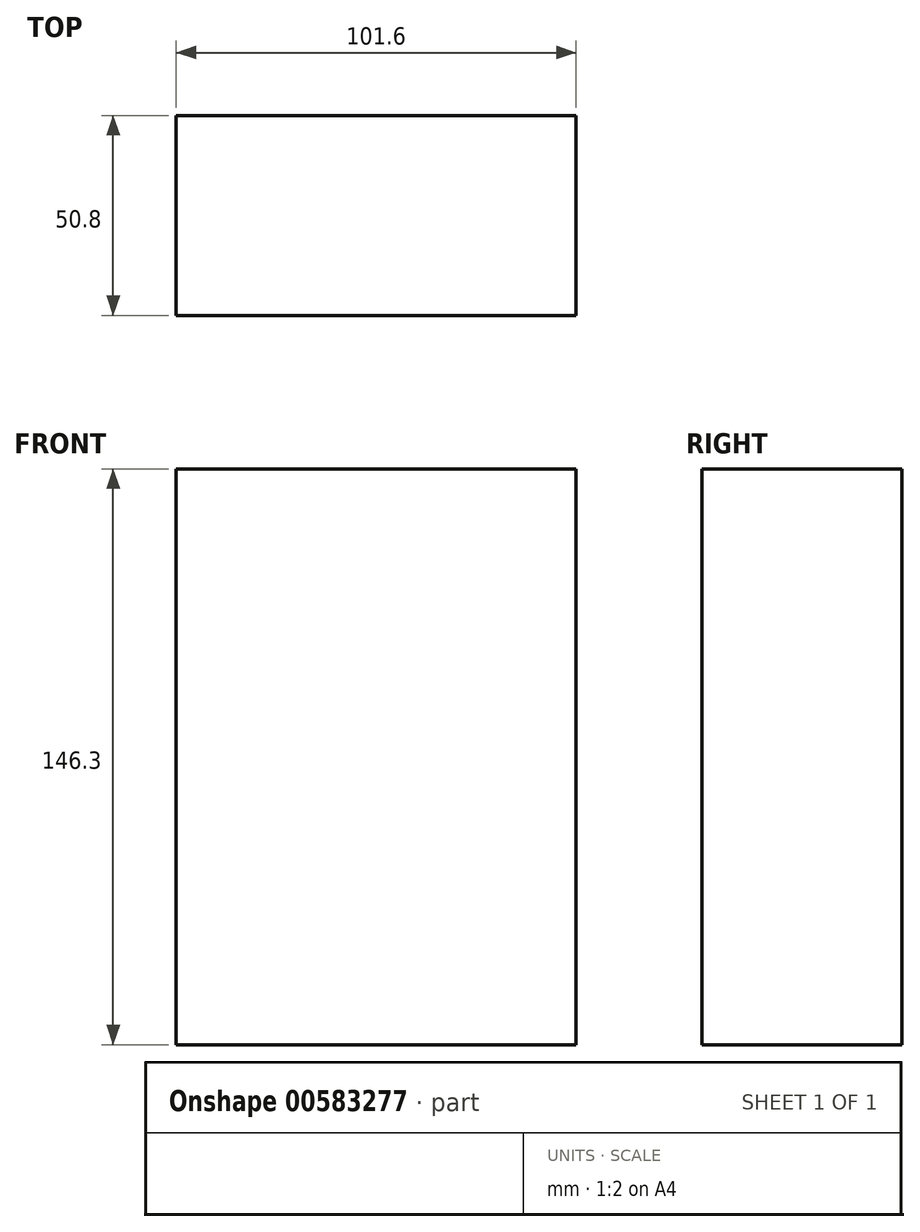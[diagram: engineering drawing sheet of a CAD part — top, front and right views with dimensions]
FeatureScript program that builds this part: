
annotation { "Feature Type Name" : "Feature", "Feature Type Description" : "" }
export const myFeature = defineFeature(function(context is Context, id is Id, definition is map)
    precondition{}
    {
        {
            var Q0;
            Q0=qCreatedBy(makeId("Top.planeOp"),FACE);
            var sketch = newSketch(context, id + "F0", { "sketchPlane" : qUnion([Q0])});
            skLineSegment(sketch, "E0.bottom", {"start": v(-48.7, 4.66) * mm, "end": v(52.9, 4.66) * mm});
            skLineSegment(sketch, "E0.top", {"start": v(-48.7, -46.14) * mm, "end": v(52.9, -46.14) * mm});
            skLineSegment(sketch, "E0.left", {"start": v(-48.7, 4.66) * mm, "end": v(-48.7, -46.14) * mm});
            skLineSegment(sketch, "E0.right", {"start": v(52.9, 4.66) * mm, "end": v(52.9, -46.14) * mm});
            skSolve(sketch);
        }
        {
            var Q0;
            Q0=makeQuery(id+"F0.imprint","IMPRINT",FACE,{"disambiguationData":[TD([[makeQuery(id+"F0.imprint","IMPRINT",EDGE,{"derivedFrom":sQuery(id+"F0.wireOp",EDGE,"E0.bottom")}),-1.0]])]});
            extrude(context, id + "F1", {"entities" : qUnion([Q0]), "depth" : 146.3 * mm, "offsetDistance" : 25.4 * mm});
        }
    });
